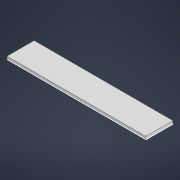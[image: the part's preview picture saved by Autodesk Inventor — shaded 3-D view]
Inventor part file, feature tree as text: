
AUTODESK INVENTOR PART (.ipt)
format: ipt  version: 2022 (Build 260153000, 153)  size: 86,528 bytes
history: native  units: mm
features: other x1, extrude x1
ambient origin geometry x8: Origin, YZ Plane, XZ Plane, XY Plane, X Axis, Y Axis, Z Axis, Center Point
bodies: Body1 (feature_tree)
feature tree (2):
  other  "Твердое тело1"
  extrude  "Выдавливание1"  Depth=12.0mm TaperAngle=0.0deg
